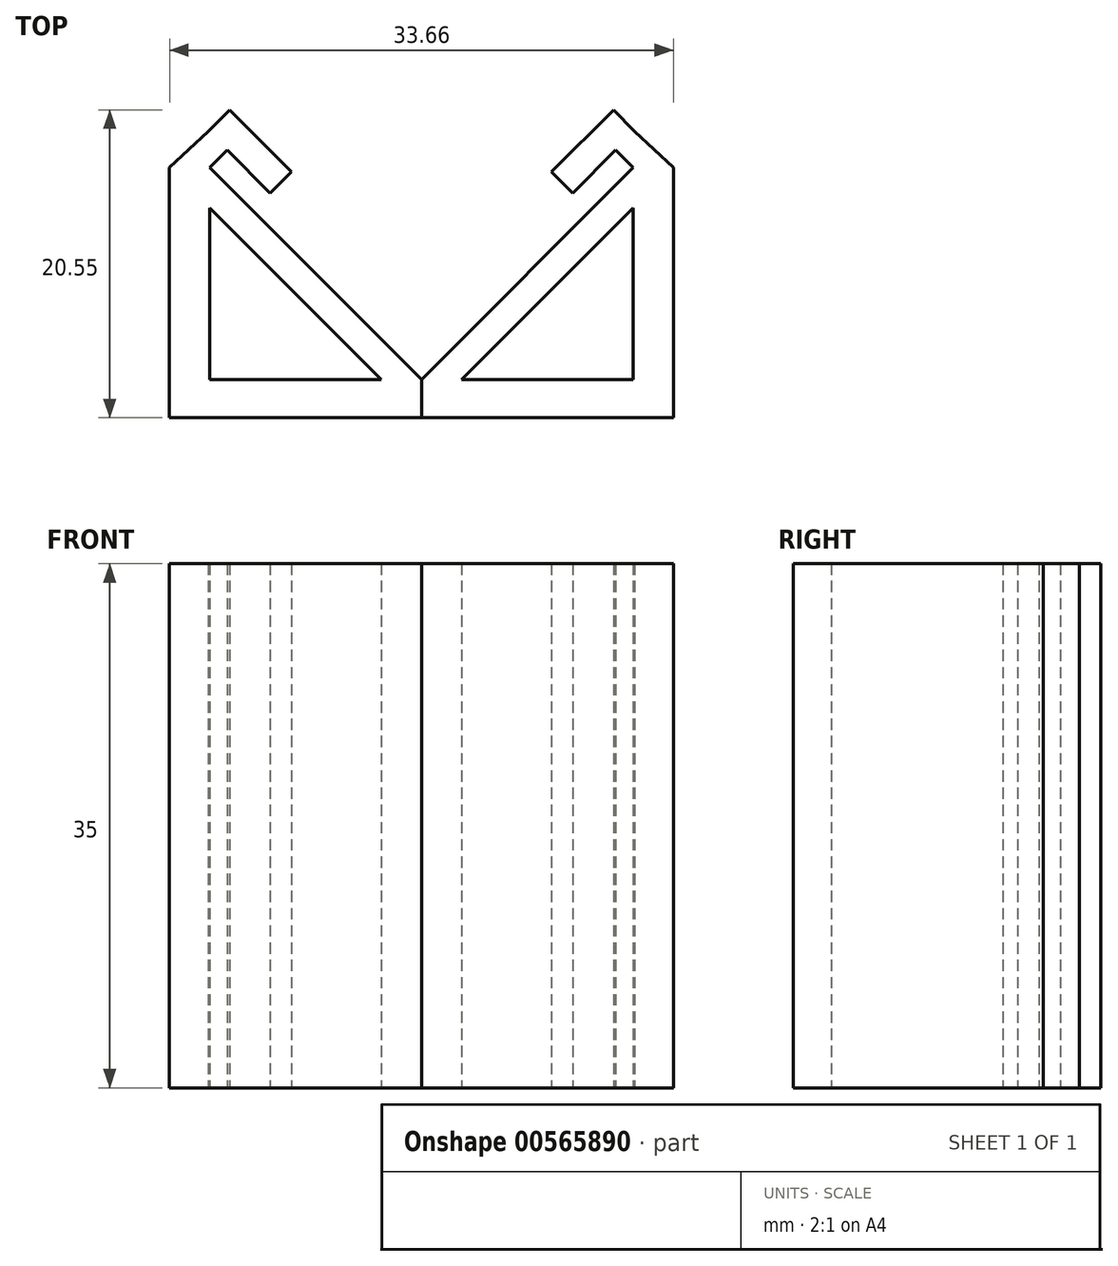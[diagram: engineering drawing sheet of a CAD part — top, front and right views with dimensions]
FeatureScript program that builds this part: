
annotation { "Feature Type Name" : "Feature", "Feature Type Description" : "" }
export const myFeature = defineFeature(function(context is Context, id is Id, definition is map)
    precondition{}
    {
        {
            var Q0;
            Q0=qCreatedBy(makeId("Top.planeOp"),FACE);
            var sketch = newSketch(context, id + "F0", { "sketchPlane" : qUnion([Q0])});
            skLineSegment(sketch, "E0", {"start": v(0, 0) * mm, "end": v(14.14, 14.14) * mm});
            skLineSegment(sketch, "E1", {"start": v(14.14, 11.45) * mm, "end": v(14.14, 0) * mm});
            skLineSegment(sketch, "E2", {"start": v(14.14, 0) * mm, "end": v(2.69, 0) * mm});
            skLineSegment(sketch, "E3", {"start": v(2.69, 0) * mm, "end": v(14.14, 11.45) * mm});
            skLineSegment(sketch, "E4", {"start": v(16.83, 14.14) * mm, "end": v(16.83, -2.56) * mm});
            skLineSegment(sketch, "E5", {"start": v(16.83, -2.56) * mm, "end": v(0, -2.56) * mm});
            skLineSegment(sketch, "E6", {"start": v(0, -2.56) * mm, "end": v(0, 0) * mm});
            skLineSegment(sketch, "E7", {"start": v(14.14, 14.14) * mm, "end": v(12.98, 15.3) * mm});
            skLineSegment(sketch, "E8", {"start": v(14.24, 16.57) * mm, "end": v(16.83, 14.14) * mm});
            skLineSegment(sketch, "E9", {"start": v(14.24, 16.57) * mm, "end": v(12.82, 17.99) * mm});
            skLineSegment(sketch, "E10", {"start": v(12.82, 17.99) * mm, "end": v(8.7, 13.86) * mm});
            skLineSegment(sketch, "E11", {"start": v(8.7, 13.86) * mm, "end": v(10.1, 12.44) * mm});
            skLineSegment(sketch, "E12", {"start": v(10.1, 12.44) * mm, "end": v(12.98, 15.3) * mm});
            skSolve(sketch);
        }
        {
            var Q0;
            Q0=qCreatedBy(makeId("Top.planeOp"),FACE);
            var sketch = newSketch(context, id + "F1", { "sketchPlane" : qUnion([Q0])});
            skLineSegment(sketch, "E13.0.0", {"start": v(14.24, 16.57) * mm, "end": v(12.82, 17.99) * mm});
            skLineSegment(sketch, "E13.0.1", {"start": v(12.82, 17.99) * mm, "end": v(8.7, 13.86) * mm});
            skLineSegment(sketch, "E13.0.2", {"start": v(8.7, 13.86) * mm, "end": v(10.1, 12.44) * mm});
            skLineSegment(sketch, "E13.0.3", {"start": v(10.1, 12.44) * mm, "end": v(12.98, 15.3) * mm});
            skLineSegment(sketch, "E13.0.4", {"start": v(12.98, 15.3) * mm, "end": v(14.14, 14.14) * mm});
            skLineSegment(sketch, "E13.0.5", {"start": v(14.14, 14.14) * mm, "end": v(0, 0) * mm});
            skLineSegment(sketch, "E13.0.6", {"start": v(0, 0) * mm, "end": v(0, -2.56) * mm});
            skLineSegment(sketch, "E13.0.7", {"start": v(0, -2.56) * mm, "end": v(16.83, -2.56) * mm});
            skLineSegment(sketch, "E13.0.8", {"start": v(16.83, -2.56) * mm, "end": v(16.83, 14.14) * mm});
            skLineSegment(sketch, "E13.0.9", {"start": v(16.83, 14.14) * mm, "end": v(14.24, 16.57) * mm});
            skLineSegment(sketch, "E14.MirrorCS", {"start": v(-16.83, 14.14) * mm, "end": v(-14.24, 16.57) * mm});
            skLineSegment(sketch, "E15.MirrorCS", {"start": v(-16.83, -2.56) * mm, "end": v(-16.83, 14.14) * mm});
            skLineSegment(sketch, "E16.MirrorCS", {"start": v(0, -2.56) * mm, "end": v(-16.83, -2.56) * mm});
            skLineSegment(sketch, "E17.MirrorCS", {"start": v(-14.14, 14.14) * mm, "end": v(0, 0) * mm});
            skLineSegment(sketch, "E18.MirrorCS", {"start": v(-12.98, 15.3) * mm, "end": v(-14.14, 14.14) * mm});
            skLineSegment(sketch, "E19.MirrorCS", {"start": v(-10.1, 12.44) * mm, "end": v(-12.98, 15.3) * mm});
            skLineSegment(sketch, "E20.MirrorCS", {"start": v(-8.7, 13.86) * mm, "end": v(-10.1, 12.44) * mm});
            skLineSegment(sketch, "E21.MirrorCS", {"start": v(-12.82, 17.99) * mm, "end": v(-8.7, 13.86) * mm});
            skLineSegment(sketch, "E22.MirrorCS", {"start": v(-14.24, 16.57) * mm, "end": v(-12.82, 17.99) * mm});
            skLineSegment(sketch, "E23.0", {"start": v(2.69, 0) * mm, "end": v(14.14, 11.45) * mm});
            skLineSegment(sketch, "E23.1", {"start": v(14.14, 0) * mm, "end": v(2.69, 0) * mm});
            skLineSegment(sketch, "E23.2", {"start": v(14.14, 11.45) * mm, "end": v(14.14, 0) * mm});
            skLineSegment(sketch, "E24.MirrorCS", {"start": v(-2.69, 0) * mm, "end": v(-14.14, 11.45) * mm});
            skLineSegment(sketch, "E25.MirrorCS", {"start": v(-14.14, 0) * mm, "end": v(-2.69, 0) * mm});
            skLineSegment(sketch, "E26.MirrorCS", {"start": v(-14.14, 11.45) * mm, "end": v(-14.14, 0) * mm});
            skSolve(sketch);
        }
        {
            var Q0;
            Q0=makeQuery(id+"F1.imprint","IMPRINT",FACE,{"disambiguationData":[TD([[makeQuery(id+"F1.imprint","IMPRINT",EDGE,{"derivedFrom":sQuery(id+"F1.wireOp",EDGE,"E13.0.6")}),-1.0]])]});
            var Q1;
            Q1=makeQuery(id+"F0.imprint","IMPRINT",FACE,{"disambiguationData":[TD([[makeQuery(id+"F0.imprint","IMPRINT",EDGE,{"derivedFrom":sQuery(id+"F0.wireOp",EDGE,"E0")}),-1.0]])]});
            extrude(context, id + "F2", {"entities" : qUnion([Q0, Q1]), "depth" : 35 * mm, "offsetDistance" : 25 * mm});
        }
    });
